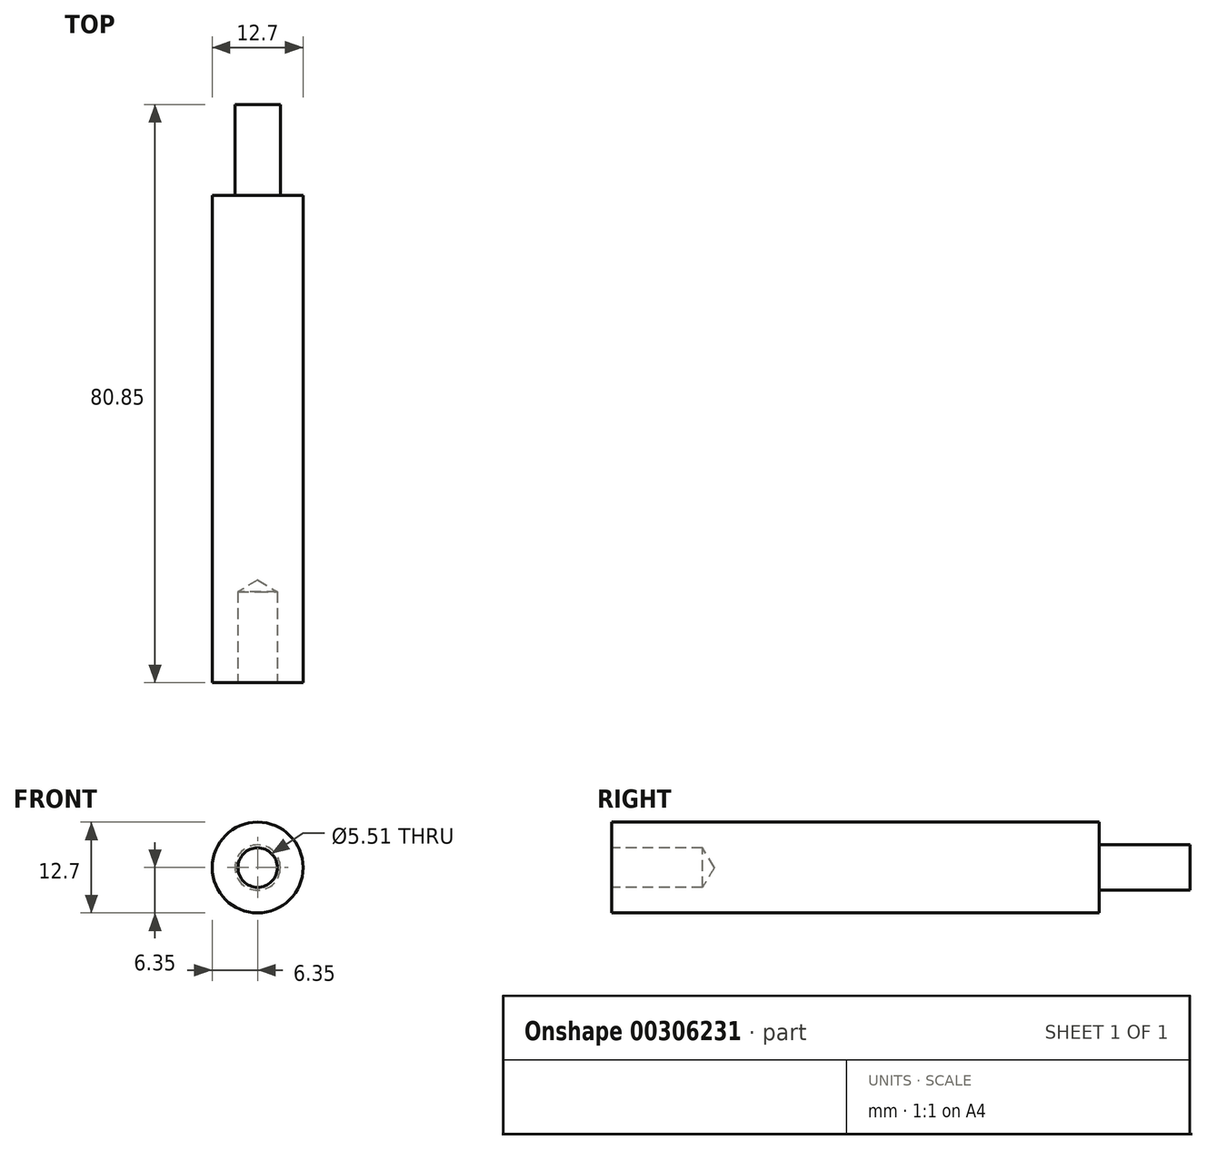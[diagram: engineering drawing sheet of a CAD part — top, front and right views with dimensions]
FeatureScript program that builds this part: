
annotation { "Feature Type Name" : "Feature", "Feature Type Description" : "" }
export const myFeature = defineFeature(function(context is Context, id is Id, definition is map)
    precondition{}
    {
        {
            var Q0;
            Q0=qCreatedBy(makeId("Front.planeOp"),FACE);
            var sketch = newSketch(context, id + "F0", { "sketchPlane" : qUnion([Q0])});
            skCircle(sketch, "E0", {"center": v(0, 0) * mm, "radius": 3.18 * mm});
            skSolve(sketch);
        }
        {
            var Q0;
            Q0 = qSketchRegion(id + "F0", true);
            extrude(context, id + "F1", {"entities" : qUnion([Q0]), "depth" : 12.7 * mm});
        }
        {
            var Q0;
            Q0=makeQuery(id+"F1.opExtrude","CAP_FACE",FACE,{"disambiguationData":[OSD([sQuery(id+"F0.wireOp",EDGE,"E0")])],"isStart":false});
            var sketch = newSketch(context, id + "F2", { "sketchPlane" : qUnion([Q0])});
            skCircle(sketch, "E1", {"center": v(0, 0) * mm, "radius": 6.35 * mm});
            skSolve(sketch);
        }
        {
            var Q0;
            Q0 = qSketchRegion(id + "F2", true);
            extrude(context, id + "F3", {"entities" : qUnion([Q0]), "operationType" : NewBodyOperationType.ADD, "depth" : 68.15 * mm});
        }
        {
            var Q0;
            Q0=makeQuery(id+"F3.opExtrude","CAP_FACE",FACE,{"disambiguationData":[OSD([sQuery(id+"F2.wireOp",EDGE,"E1")])],"isStart":false});
            var sketch = newSketch(context, id + "F4", { "sketchPlane" : qUnion([Q0])});
            skPoint(sketch, "E2", {"position": v(0, 0) * mm});
            skSolve(sketch);
        }
        {
            var Q0;
            Q0=sQuery(id+"F4.wireOp",VERTEX,"E2");
            var Q1;
            Q1=makeQuery(id+"F1.opExtrude","SWEPT_BODY",BODY,{"disambiguationData":[OSD([sQuery(id+"F0.wireOp",EDGE,"E0")])]});
            hole(context, id + "F5", {"style" : HoleStyle.SIMPLE, "endStyle" : HoleEndStyle.BLIND, "holeDiameter" : 5.5 * mm, "holeDepth" : 12.7 * mm, "tappedDepth" : 12.7 * mm, "tapClearance" : 3, "locations" : qUnion([Q0]), "scope" : qUnion([Q1])});
        }
    });
